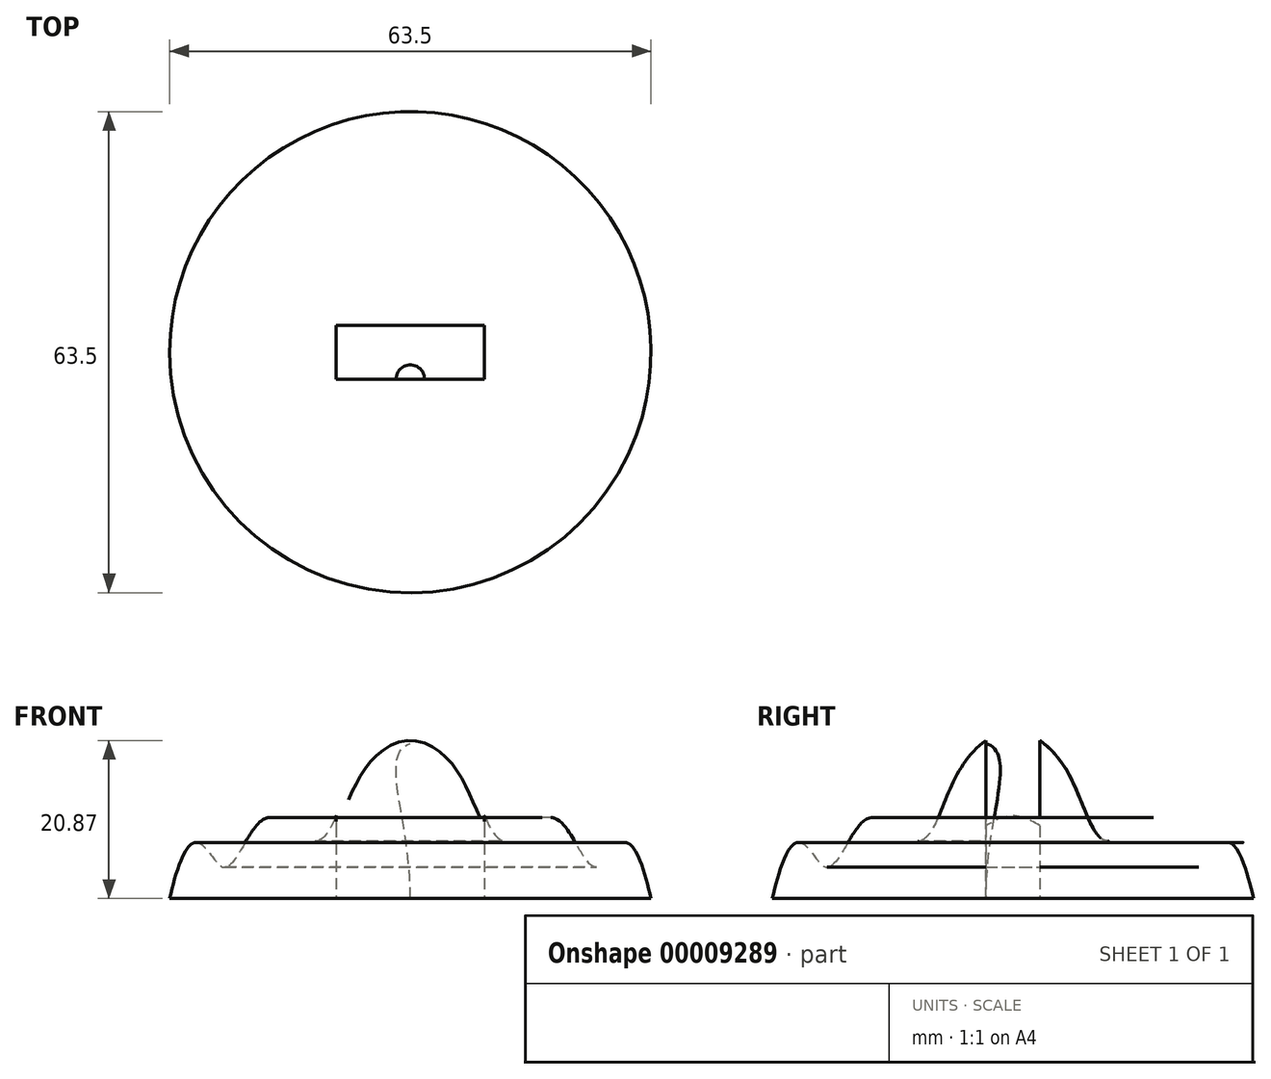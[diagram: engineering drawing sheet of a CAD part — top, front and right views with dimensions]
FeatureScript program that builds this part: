
annotation { "Feature Type Name" : "Feature", "Feature Type Description" : "" }
export const myFeature = defineFeature(function(context is Context, id is Id, definition is map)
    precondition{}
    {
        {
            var Q0;
            Q0=qCreatedBy(makeId("Front.planeOp"),FACE);
            var sketch = newSketch(context, id + "F0", { "sketchPlane" : qUnion([Q0])});
            skLineSegment(sketch, "E0", {"start": v(0, 0) * mm, "end": v(31.75, 0) * mm});
            skLineSegment(sketch, "E1", {"start": v(0, 0) * mm, "end": v(0, 22.1) * mm});
            skLineSegment(sketch, "E2", {"start": v(0, 0) * mm, "end": v(0, 47.07) * mm, "construction": true});
            skFitSpline(sketch, "E3", {"points": [v(0, 22.1) * mm, v(7.4, 16.36) * mm, v(12.62, 7.6) * mm, v(19.14, 10.57) * mm, v(24.92, 4.24) * mm, v(31.75, 0) * mm], "startDerivative": vector(38.89, 0) * mm, "endDerivative": vector(46.32, -201.59) * mm});
            skSolve(sketch);
        }
        {
            var Q0;
            Q0=makeQuery(id+"F0.imprint","IMPRINT",FACE,{"disambiguationData":[TD([[makeQuery(id+"F0.imprint","IMPRINT",EDGE,{"derivedFrom":sQuery(id+"F0.wireOp",EDGE,"E0")}),1.0]])]});
            var Q1;
            Q1=sQuery(id+"F0.wireOp",EDGE,"E3");
            var Q2;
            Q2=sQuery(id+"F0.wireOp",EDGE,"E0");
            var Q3;
            Q3=sQuery(id+"F0.wireOp",EDGE,"E2");
            revolve(context, id + "F1", {"entities" : qUnion([Q0]), "surfaceEntities" : qUnion([Q1, Q2]), "axis" : qUnion([Q3]), "revolveType" : RevolveType.FULL});
        }
        {
            var Q0;
            Q0=qCreatedBy(makeId("Top.planeOp"),FACE);
            var sketch = newSketch(context, id + "F2", { "sketchPlane" : qUnion([Q0])});
            skLineSegment(sketch, "E4.rect.bottom", {"start": v(9.78, 3.56) * mm, "end": v(-9.78, 3.56) * mm});
            skLineSegment(sketch, "E4.rect.top", {"start": v(9.78, -3.56) * mm, "end": v(-9.78, -3.56) * mm});
            skLineSegment(sketch, "E4.rect.left", {"start": v(9.78, 3.56) * mm, "end": v(9.78, -3.56) * mm});
            skLineSegment(sketch, "E4.rect.right", {"start": v(-9.78, 3.56) * mm, "end": v(-9.78, -3.56) * mm});
            skPoint(sketch, "E4.rect.middle", {"position": v(0, 0) * mm});
            skSolve(sketch);
        }
        {
            var Q0;
            Q0=makeQuery(id+"F2.imprint","IMPRINT",FACE,{"disambiguationData":[TD([[makeQuery(id+"F2.imprint","IMPRINT",EDGE,{"derivedFrom":sQuery(id+"F2.wireOp",EDGE,"E4.rect.bottom")}),1.0]])]});
            extrude(context, id + "F3", {"entities" : qUnion([Q0]), "operationType" : NewBodyOperationType.REMOVE, "endBound" : BoundingType.THROUGH_ALL, "depth" : 25.4 * mm});
        }
        {
            var Q0;
            Q0=qCreatedBy(makeId("Right.planeOp"),FACE);
            var sketch = newSketch(context, id + "F4", { "sketchPlane" : qUnion([Q0])});
            skLineSegment(sketch, "E5.0.0", {"start": v(-3.56, 9.6) * mm, "end": v(-3.56, 0) * mm});
            skLineSegment(sketch, "E5.0.2", {"start": v(-3.56, 0) * mm, "end": v(-3.56, 9.6) * mm});
            skLineSegment(sketch, "E6.0.1", {"start": v(3.56, 9.6) * mm, "end": v(3.56, 0) * mm});
            skLineSegment(sketch, "E6.0.3", {"start": v(3.56, 0) * mm, "end": v(3.56, 9.6) * mm});
            skFitSpline(sketch, "E7", {"points": [v(-3.56, 0) * mm, v(-1.72, 17.82) * mm, v(-3.56, 20.45) * mm], "startDerivative": vector(0, 33.4) * mm, "endDerivative": vector(-10.62, 2.28) * mm});
            skLineSegment(sketch, "E8", {"start": v(-3.56, 20.45) * mm, "end": v(-3.56, 0) * mm});
            skSolve(sketch);
        }
        {
            var Q0;
            Q0 = qSketchRegion(id + "F4", true);
            var Q1;
            Q1=sQuery(id+"F4.wireOp",EDGE,"E8");
            revolve(context, id + "F5", {"operationType" : NewBodyOperationType.ADD, "entities" : qUnion([Q0]), "axis" : qUnion([Q1]), "revolveType" : RevolveType.FULL});
        }
    });
